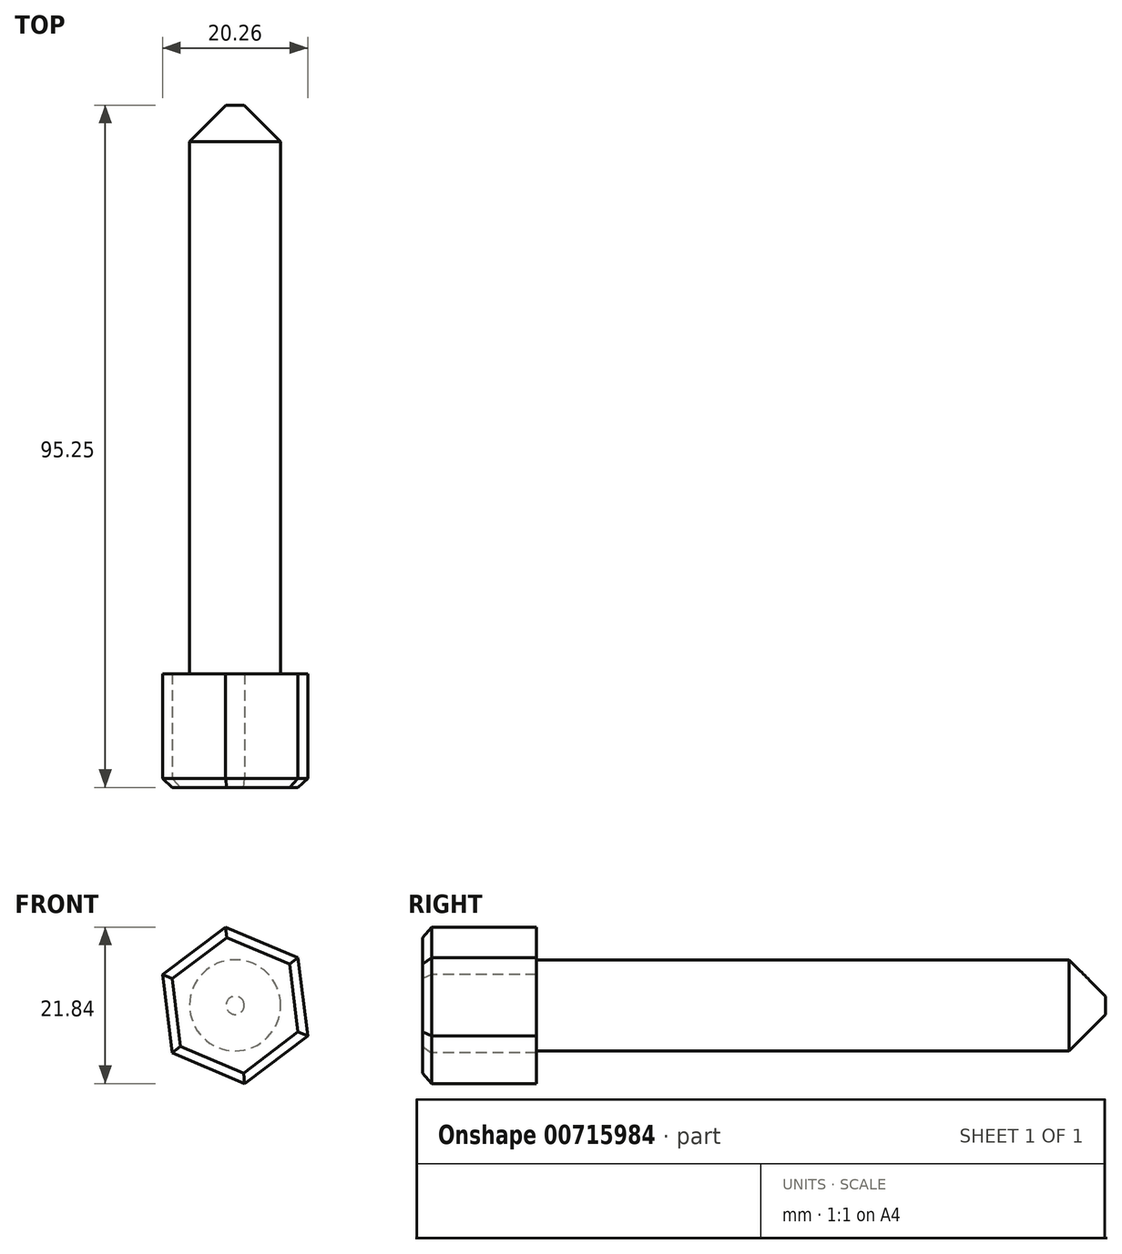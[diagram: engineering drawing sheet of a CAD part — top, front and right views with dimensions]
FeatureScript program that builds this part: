
annotation { "Feature Type Name" : "Feature", "Feature Type Description" : "" }
export const myFeature = defineFeature(function(context is Context, id is Id, definition is map)
    precondition{}
    {
        {
            var Q0;
            Q0=qCreatedBy(makeId("Front.planeOp"),FACE);
            var sketch = newSketch(context, id + "F0", { "sketchPlane" : qUnion([Q0])});
            skCircle(sketch, "E0.cCircle", {"center": v(0, 0) * mm, "radius": 9.53 * mm, "construction": true});
            skLineSegment(sketch, "E0.0", {"start": v(-10.13, 4.29) * mm, "end": v(-1.35, 10.92) * mm});
            skLineSegment(sketch, "E0.1", {"start": v(-1.35, 10.92) * mm, "end": v(8.78, 6.63) * mm});
            skLineSegment(sketch, "E0.2", {"start": v(8.78, 6.63) * mm, "end": v(10.13, -4.29) * mm});
            skLineSegment(sketch, "E0.3", {"start": v(10.13, -4.29) * mm, "end": v(1.35, -10.92) * mm});
            skLineSegment(sketch, "E0.4", {"start": v(1.35, -10.92) * mm, "end": v(-8.78, -6.63) * mm});
            skLineSegment(sketch, "E0.5", {"start": v(-8.78, -6.63) * mm, "end": v(-10.13, 4.29) * mm});
            skPoint(sketch, "E0.0.midPoint", {"position": v(-5.74, 7.6) * mm});
            skSolve(sketch);
        }
        {
            var Q0;
            Q0=makeQuery(id+"F0.imprint","IMPRINT",FACE,{"disambiguationData":[TD([[makeQuery(id+"F0.imprint","IMPRINT",EDGE,{"derivedFrom":sQuery(id+"F0.wireOp",EDGE,"E0.0")}),-1.0]])]});
            extrude(context, id + "F1", {"entities" : qUnion([Q0]), "oppositeDirection" : true, "depth" : 15.88 * mm, "offsetDistance" : 25.4 * mm});
        }
        {
            var Q0;
            Q0=makeQuery(id+"F1.opExtrude","CAP_EDGE",EDGE,{"disambiguationData":[OSD([sQuery(id+"F0.wireOp",EDGE,"E0.1")])],"isStart":true});
            var Q1;
            Q1=makeQuery(id+"F1.opExtrude","CAP_EDGE",EDGE,{"disambiguationData":[OSD([sQuery(id+"F0.wireOp",EDGE,"E0.0")])],"isStart":true});
            var Q2;
            Q2=makeQuery(id+"F1.opExtrude","CAP_EDGE",EDGE,{"disambiguationData":[OSD([sQuery(id+"F0.wireOp",EDGE,"E0.5")])],"isStart":true});
            var Q3;
            Q3=makeQuery(id+"F1.opExtrude","CAP_EDGE",EDGE,{"disambiguationData":[OSD([sQuery(id+"F0.wireOp",EDGE,"E0.4")])],"isStart":true});
            var Q4;
            Q4=makeQuery(id+"F1.opExtrude","CAP_EDGE",EDGE,{"disambiguationData":[OSD([sQuery(id+"F0.wireOp",EDGE,"E0.3")])],"isStart":true});
            var Q5;
            Q5=makeQuery(id+"F1.opExtrude","CAP_EDGE",EDGE,{"disambiguationData":[OSD([sQuery(id+"F0.wireOp",EDGE,"E0.2")])],"isStart":true});
            chamfer(context, id + "F2", {"entities" : qUnion([Q0, Q1, Q2, Q3, Q4, Q5]), "width" : 1.27 * mm, "tangentPropagation" : true});
        }
        {
            var Q0;
            Q0=makeQuery(id+"F1.opExtrude","CAP_FACE",FACE,{"disambiguationData":[OSD([sQuery(id+"F0.wireOp",EDGE,"E0.0"),sQuery(id+"F0.wireOp",EDGE,"E0.1"),sQuery(id+"F0.wireOp",EDGE,"E0.2"),sQuery(id+"F0.wireOp",EDGE,"E0.3"),sQuery(id+"F0.wireOp",EDGE,"E0.4"),sQuery(id+"F0.wireOp",EDGE,"E0.5")])],"isStart":false});
            cPlane(context, id + "F3", {"entities" : qUnion([Q0]), "cplaneType" : CPlaneType.OFFSET, "offset" : 0 * mm, "width" : 152.4 * mm, "height" : 152.4 * mm});
        }
        {
            var Q0;
            Q0=qCreatedBy(id+"F3.planeOp",FACE);
            var sketch = newSketch(context, id + "F4", { "sketchPlane" : qUnion([Q0])});
            skCircle(sketch, "E1", {"center": v(0, 0) * mm, "radius": 6.35 * mm});
            skSolve(sketch);
        }
        {
            var Q0;
            Q0 = qSketchRegion(id + "F4", true);
            extrude(context, id + "F5", {"entities" : qUnion([Q0]), "operationType" : NewBodyOperationType.ADD, "depth" : 79.38 * mm, "offsetDistance" : 25.4 * mm});
        }
        {
            var Q0;
            Q0=makeQuery(id+"F5.opExtrude","CAP_EDGE",EDGE,{"disambiguationData":[OSD([sQuery(id+"F4.wireOp",EDGE,"E1")])],"isStart":false});
            chamfer(context, id + "F6", {"entities" : qUnion([Q0]), "width" : 5.08 * mm, "tangentPropagation" : true});
        }
    });
